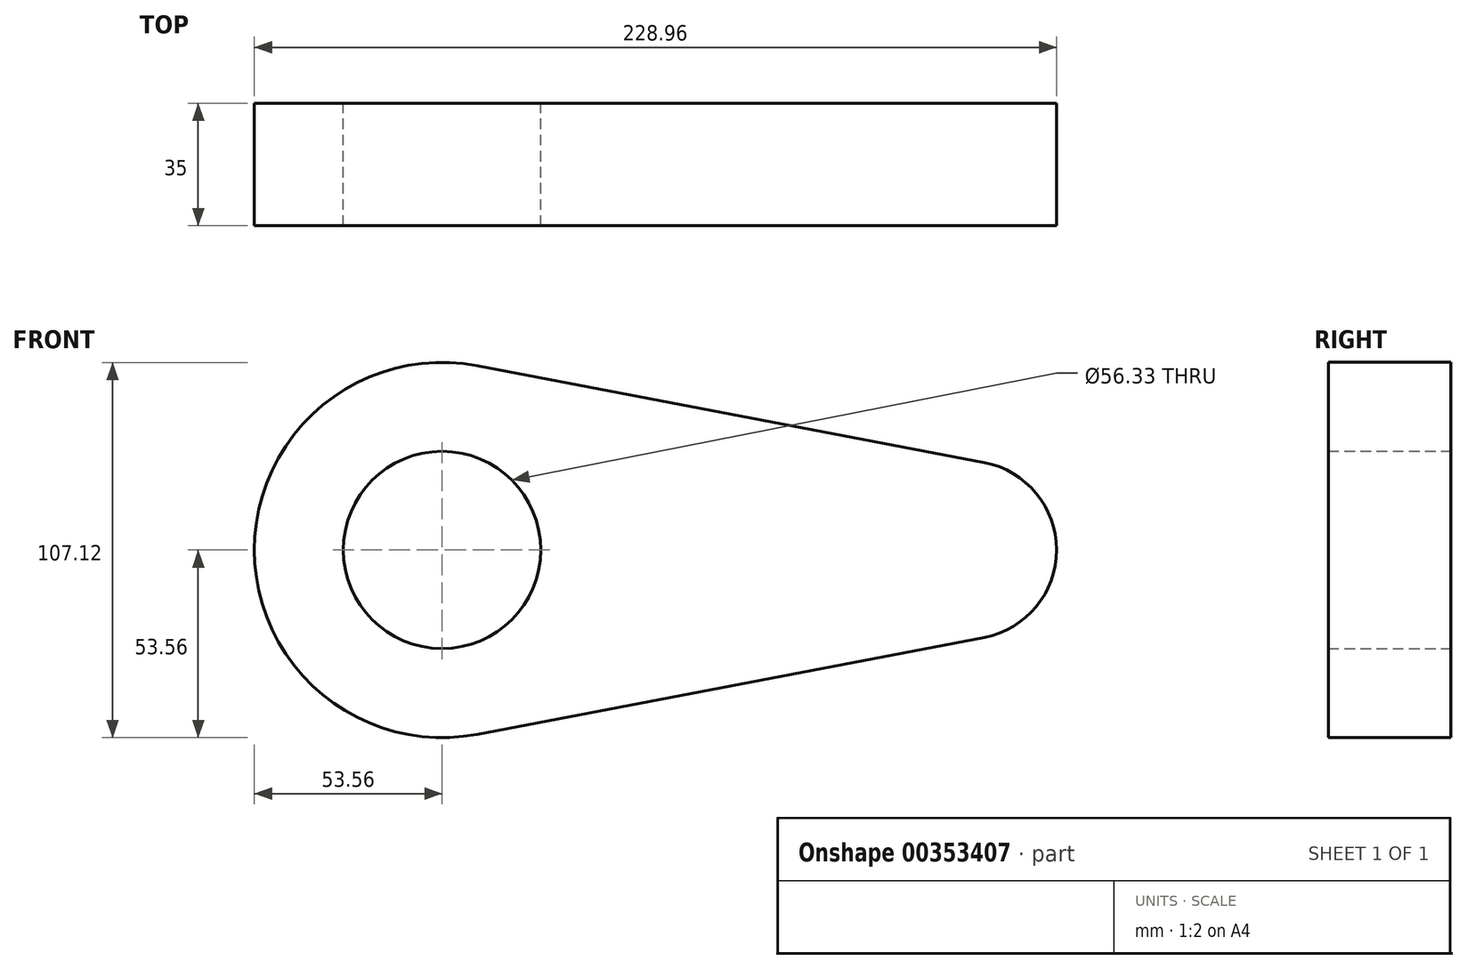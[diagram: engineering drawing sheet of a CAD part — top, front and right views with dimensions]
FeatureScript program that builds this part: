
annotation { "Feature Type Name" : "Feature", "Feature Type Description" : "" }
export const myFeature = defineFeature(function(context is Context, id is Id, definition is map)
    precondition{}
    {
        {
            var Q0;
            Q0=qCreatedBy(makeId("Front.planeOp"),FACE);
            var sketch = newSketch(context, id + "F0", { "sketchPlane" : qUnion([Q0])});
            skCircle(sketch, "E0", {"center": v(0, 0) * mm, "radius": 53.56 * mm});
            skCircle(sketch, "E1", {"center": v(150, 0) * mm, "radius": 25.4 * mm});
            skLineSegment(sketch, "E2", {"start": v(10.06, 52.61) * mm, "end": v(154.77, 24.95) * mm});
            skLineSegment(sketch, "E3", {"start": v(10.06, -52.61) * mm, "end": v(154.77, -24.95) * mm});
            skCircle(sketch, "E4", {"center": v(0, 0) * mm, "radius": 28.16 * mm});
            skSolve(sketch);
        }
        {
            var Q0;
            {var subQ0=sQuery(id+"F0.wireOp",EDGE,"E2");Q0=makeQuery(id+"F0.imprint","IMPRINT",FACE,{"disambiguationData":[TD([[makeQuery(id+"F0.imprint","IMPRINT",EDGE,{"derivedFrom":subQ0}),-1.0]])]});}
            var Q1;
            Q1=makeQuery(id+"F0.imprint","IMPRINT",FACE,{"disambiguationData":[TD([[makeQuery(id+"F0.imprint","IMPRINT",EDGE,{"derivedFrom":sQuery(id+"F0.wireOp",EDGE,"E4")}),-1.0]])]});
            var Q2;
            {var subQ0=sQuery(id+"F0.wireOp",EDGE,"E1");var subQ1=makeQuery(id+"F0.imprint","INTERSECT",VERTEX,{"derivedFrom":[subQ0,sQuery(id+"F0.wireOp",EDGE,"E2")]});Q2=makeQuery(id+"F0.imprint","IMPRINT",FACE,{"disambiguationData":[TD([[makeQuery(id+"F0.imprint","IMPRINT",EDGE,{"disambiguationData":[TD([[subQ1,-1.0]])],"derivedFrom":subQ0}),1.0]])]});}
            extrude(context, id + "F1", {"entities" : qUnion([Q0, Q1, Q2]), "depth" : 35 * mm});
        }
        {
            var Q0;
            Q0=makeQuery(id+"F1.opExtrude","SWEPT_FACE",FACE,{"disambiguationData":[OSD([sQuery(id+"F0.wireOp",EDGE,"E2")])]});
            var sketch = newSketch(context, id + "F2", { "sketchPlane" : qUnion([Q0])});
            skCircle(sketch, "E5", {"center": v(73.67, -17.4) * mm, "radius": 12.24 * mm});
            skPoint(sketch, "E5.centerSnap0", {"position": v(73.67, 0) * mm});
            skSolve(sketch);
        }
        {
            var Q0;
            Q0=sQuery(id+"F2.wireOp",EDGE,"E5");
            extrude(context, id + "F3", {"bodyType" : ToolBodyType.SURFACE, "surfaceEntities" : qUnion([Q0]), "depth" : 19 * mm});
        }
    });
